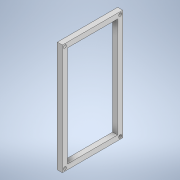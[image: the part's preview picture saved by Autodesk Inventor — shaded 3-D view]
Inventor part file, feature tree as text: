
AUTODESK INVENTOR PART (.ipt)
format: ipt  version: 2021 (Build 250183000, 183)  size: 116,736 bytes
history: native  units: mm
features: extrude x1, sketch x1
ambient origin geometry x8: Origin, YZ Plane, XZ Plane, XY Plane, X Axis, Y Axis, Z Axis, Center Point
bodies: Solide1 (feature_tree)
feature tree (2):
  extrude  "Extrusion1"  Depth=10.0mm
  sketch  "Esquisse1"
